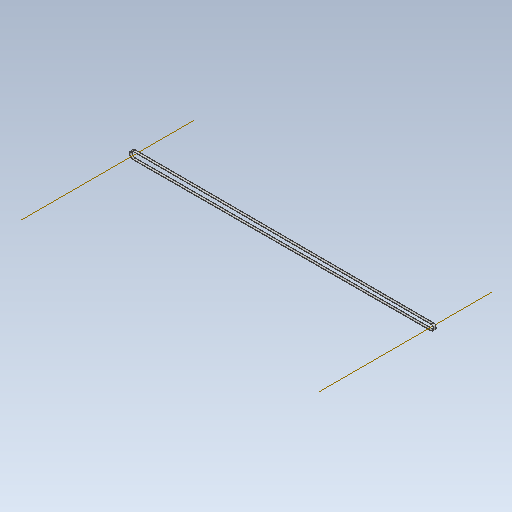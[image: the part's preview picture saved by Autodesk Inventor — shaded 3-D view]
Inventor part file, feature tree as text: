
AUTODESK INVENTOR PART (.ipt)
format: ipt  version: 2020 (Build 240168000, 168)  size: 93,184 bytes
history: native  units: mm (DEFAULTED — no unit token found)
features: other x4, plane x2, sketch x1, sweep x1
ambient origin geometry x8: Origin, YZ Plane, XZ Plane, XY Plane, X Axis, Y Axis, Z Axis, Center Point
bodies: Solid1 (feature_tree)
feature tree (8):
  sketch  "Sketch Path"  dims[d0=4.0mm d2=0.0mm d4=0.3mm d5=0.3mm d6=0.0mm d7=0.0mm d8=0.0mm d9=0.0mm d10=0.0mm d11=0.0mm]
  other  "Cross Section Plane"
  other  "Work Axis1"
  other  "Work Axis2"
  plane  "Work Plane2"
  plane  "Work Plane3"
  sweep  "Belt"
  other  "Cross Section"
